# Revit family: IVLB_Generic_LF_Wall Mounted Luminaire Round
name_source: partatom
category: Lighting Fixtures
units: mm (PartAtom-declared; Revit-internal decimal feet)

## family parameters
Always vertical = Yes
Cut with Voids When Loaded = No
Light Source = No
OmniClass Number = 23.80.70.11.14.11
OmniClass Title = Downlights
Part Type = Normal
Room Calculation Point = Yes
Round Connector Dimension = Use Diameter
Shared = No
Work Plane-Based = No

## types (1)
- Generic Wall Luminaire Round
    43mm Height = Yes
    63mm Height = No
    Apparent Load = 18 VA
    Assembly Code = 63.0
    Bundle = 110°
    Description = Surface Mounted
    Diameter = 300 mm
    IfcExportAs = IfcLightFixtureType
    IfcExportType = USERDEFINED
    Lamp = LED
    Light Source = Generic Lightsource
    Luminaire_Body_Material = PPS Plastic
    Manufacturer = ETK licht B.V.
    Model = FMK.1
    Radius = 150 mm
    Type Comments = IP20
    URL = https://www.etk.nl
    Voltage = 230 V
    Wattage Comments = 18W

## geometry (parser evidence)
native form markers: Sweep x8
no freeform markers — native parametric forms only
